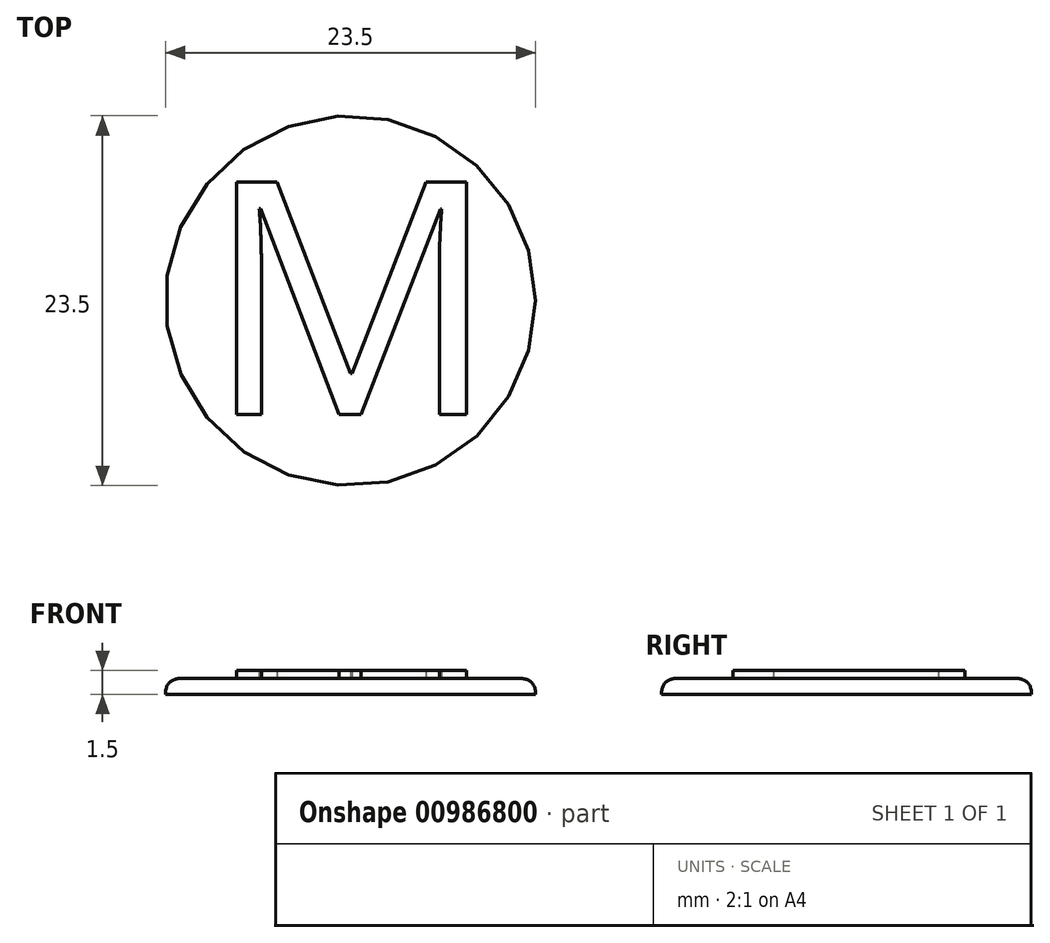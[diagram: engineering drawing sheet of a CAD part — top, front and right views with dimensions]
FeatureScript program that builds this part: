
annotation { "Feature Type Name" : "Feature", "Feature Type Description" : "" }
export const myFeature = defineFeature(function(context is Context, id is Id, definition is map)
    precondition{}
    {
        {
            var Q0;
            Q0=qCreatedBy(makeId("Top.planeOp"),FACE);
            var sketch = newSketch(context, id + "F0", { "sketchPlane" : qUnion([Q0])});
            skCircle(sketch, "E0", {"center": v(0, 0) * mm, "radius": 11.75 * mm});
            skSolve(sketch);
        }
        {
            var Q0;
            Q0=makeQuery(id+"F0.imprint","IMPRINT",FACE,{"disambiguationData":[TD([[makeQuery(id+"F0.imprint","IMPRINT",EDGE,{"derivedFrom":sQuery(id+"F0.wireOp",EDGE,"E0")}),1.0]])]});
            extrude(context, id + "F1", {"entities" : qUnion([Q0]), "depth" : 1 * mm, "offsetDistance" : 25 * mm});
        }
        {
            var Q0;
            Q0=makeQuery(id+"F1.opExtrude","CAP_FACE",FACE,{"disambiguationData":[OSD([sQuery(id+"F0.wireOp",EDGE,"E0")])],"isStart":false});
            var sketch = newSketch(context, id + "F2", { "sketchPlane" : qUnion([Q0])});
            skText(sketch, "E1", { "text": "M", "fontName": "OpenSans-Regular.ttf"});
            const initialGuessF2  = {"E1": [-0.00927, -0.00722, 1, 0, 0.01487]};
            skSetInitialGuess(sketch, initialGuessF2);
            skSolve(sketch);
        }
        {
            var Q0;
            Q0=qSketchRegion(id+"F2",true);
            extrude(context, id + "F3", {"entities" : qUnion([Q0]), "operationType" : NewBodyOperationType.ADD, "depth" : 0.5 * mm, "offsetDistance" : 25 * mm});
        }
        {
            var Q0;
            Q0=makeQuery(id+"F1.opExtrude","CAP_EDGE",EDGE,{"disambiguationData":[OSD([sQuery(id+"F0.wireOp",EDGE,"E0")])],"isStart":false});
            fillet(context, id + "F4", {"entities" : qUnion([Q0]), "radius" : 1 * mm, "tangentPropagation" : true, "rho" : 0.5, "crossSection" : FilletCrossSection.CONIC, "allowEdgeOverflow" : false});
        }
    });
